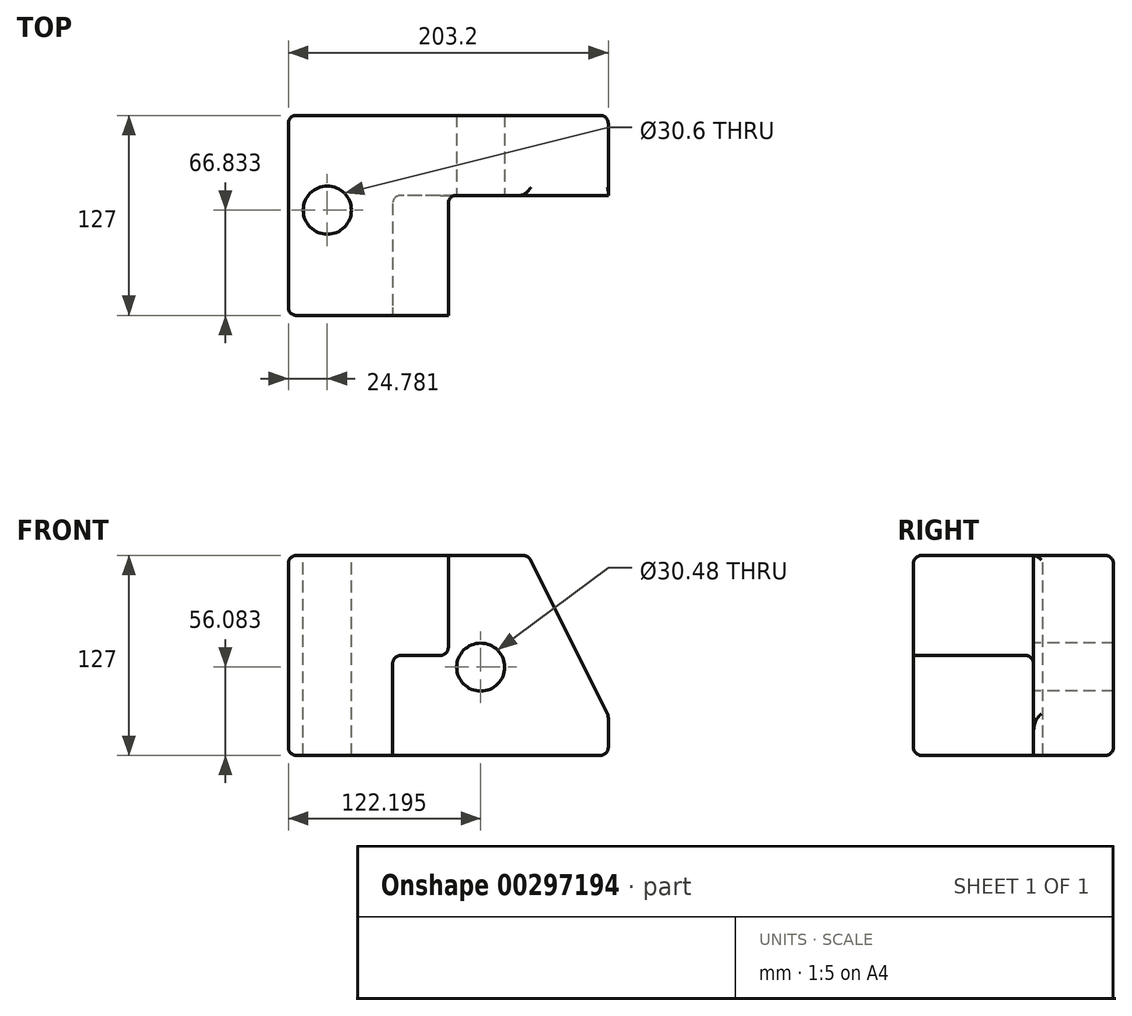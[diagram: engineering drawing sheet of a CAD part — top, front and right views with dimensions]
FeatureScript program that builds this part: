
annotation { "Feature Type Name" : "Feature", "Feature Type Description" : "" }
export const myFeature = defineFeature(function(context is Context, id is Id, definition is map)
    precondition{}
    {
        {
            var Q0;
            Q0=qCreatedBy(makeId("Front.planeOp"),FACE);
            var sketch = newSketch(context, id + "F0", { "sketchPlane" : qUnion([Q0])});
            skLineSegment(sketch, "E0.bottom", {"start": v(101.6, -63.5) * mm, "end": v(-101.6, -63.5) * mm});
            skLineSegment(sketch, "E0.top", {"start": v(101.6, 63.5) * mm, "end": v(-101.6, 63.5) * mm});
            skLineSegment(sketch, "E0.left", {"start": v(101.6, -63.5) * mm, "end": v(101.6, 63.5) * mm});
            skLineSegment(sketch, "E0.right", {"start": v(-101.6, -63.5) * mm, "end": v(-101.6, 63.5) * mm});
            skPoint(sketch, "E0.middle", {"position": v(0, 0) * mm});
            skSolve(sketch);
        }
        {
            var Q0;
            Q0=makeQuery(id+"F0.imprint","IMPRINT",FACE,{"disambiguationData":[TD([[makeQuery(id+"F0.imprint","IMPRINT",EDGE,{"derivedFrom":sQuery(id+"F0.wireOp",EDGE,"E0.bottom")}),-1.0]])]});
            extrude(context, id + "F1", {"entities" : qUnion([Q0]), "depth" : 127 * mm});
        }
        {
            var Q0;
            Q0=makeQuery(id+"F1.opExtrude","CAP_FACE",FACE,{"disambiguationData":[OSD([sQuery(id+"F0.wireOp",EDGE,"E0.bottom"),sQuery(id+"F0.wireOp",EDGE,"E0.top"),sQuery(id+"F0.wireOp",EDGE,"E0.left"),sQuery(id+"F0.wireOp",EDGE,"E0.right")])],"isStart":false});
            var sketch = newSketch(context, id + "F2", { "sketchPlane" : qUnion([Q0])});
            skLineSegment(sketch, "E1", {"start": v(-101.6, 63.5) * mm, "end": v(0, 63.5) * mm});
            skLineSegment(sketch, "E2", {"start": v(0, 63.5) * mm, "end": v(0, 0) * mm});
            skLineSegment(sketch, "E3", {"start": v(0, 0) * mm, "end": v(-35.28, 0) * mm});
            skLineSegment(sketch, "E4", {"start": v(-35.28, 0) * mm, "end": v(-35.28, -63.5) * mm});
            skLineSegment(sketch, "E5", {"start": v(-35.28, -63.5) * mm, "end": v(-101.6, -63.5) * mm});
            skLineSegment(sketch, "E6", {"start": v(-101.6, -63.5) * mm, "end": v(-101.6, 63.5) * mm});
            skSolve(sketch);
        }
        {
            var Q0;
            {var subQ3=sQuery(id+"F2.wireOp",EDGE,"E2");Q0=makeQuery(id+"F2.imprint","IMPRINT",FACE,{"disambiguationData":[TD([[makeQuery(id+"F2.imprint","IMPRINT",EDGE,{"derivedFrom":subQ3}),1.0]])]});}
            extrude(context, id + "F3", {"entities" : qUnion([Q0]), "operationType" : NewBodyOperationType.REMOVE, "oppositeDirection" : true, "depth" : 76.2 * mm});
        }
        {
            var Q0;
            Q0=makeQuery(id+"F1.opExtrude","SWEPT_EDGE",EDGE,{"disambiguationData":[OSD([sQuery(id+"F0.wireOp",EDGE,"E0.top"),sQuery(id+"F0.wireOp",EDGE,"E0.left")])]});
            chamfer(context, id + "F4", {"entities" : qUnion([Q0]), "chamferType" : ChamferType.TWO_OFFSETS, "width1" : 50.8 * mm, "oppositeDirection" : false, "width2" : 101.6 * mm, "tangentPropagation" : true});
        }
        {
            var Q0;
            Q0=makeQuery(id+"F1.opExtrude","CAP_EDGE",EDGE,{"disambiguationData":[OSD([sQuery(id+"F0.wireOp",EDGE,"E0.top")])],"isStart":false});
            var Q1;
            Q1=makeQuery(id+"F3.boolean.opBoolean","COPY",EDGE,{"derivedFrom":makeQuery(id+"F3.opExtrude","SWEPT_EDGE",EDGE,{"disambiguationData":[OSD([sQuery(id+"F0.wireOp",EDGE,"E0.top"),sQuery(id+"F2.wireOp",EDGE,"E1"),sQuery(id+"F2.wireOp",EDGE,"E2")])]})});
            var Q2;
            {var subQ0=sQuery(id+"F0.wireOp",EDGE,"E0.left");var subQ1=sQuery(id+"F0.wireOp",EDGE,"E0.top");Q2=makeQuery(id+"F4.opChamfer","BLEND_EDGE",EDGE,{"blendedFrom":[makeQuery(id+"F1.opExtrude","SWEPT_EDGE",EDGE,{"disambiguationData":[OSD([subQ1,subQ0])]}),makeQuery(id+"F3.boolean.opBoolean","COPY",FACE,{"derivedFrom":makeQuery(id+"F3.opExtrude","CAP_FACE",FACE,{"disambiguationData":[OSD([sQuery(id+"F0.wireOp",EDGE,"E0.bottom"),subQ1,subQ0,sQuery(id+"F2.wireOp",EDGE,"E2"),sQuery(id+"F2.wireOp",EDGE,"E3"),sQuery(id+"F2.wireOp",EDGE,"E4")])],"isStart":false})})],"blendedInto":[makeQuery(id+"F3.boolean.opBoolean","COPY",FACE,{"derivedFrom":makeQuery(id+"F3.opExtrude","CAP_FACE",FACE,{"disambiguationData":[OSD([sQuery(id+"F0.wireOp",EDGE,"E0.bottom"),subQ1,subQ0,sQuery(id+"F2.wireOp",EDGE,"E2"),sQuery(id+"F2.wireOp",EDGE,"E3"),sQuery(id+"F2.wireOp",EDGE,"E4")])],"isStart":false})})]});}
            var Q3;
            Q3=makeQuery(id+"F1.opExtrude","SWEPT_EDGE",EDGE,{"disambiguationData":[OSD([sQuery(id+"F0.wireOp",EDGE,"E0.top"),sQuery(id+"F0.wireOp",EDGE,"E0.right")])]});
            var Q4;
            Q4=makeQuery(id+"F1.opExtrude","CAP_EDGE",EDGE,{"disambiguationData":[OSD([sQuery(id+"F0.wireOp",EDGE,"E0.top")])],"isStart":true});
            var Q5;
            {var subQ0=sQuery(id+"F0.wireOp",EDGE,"E0.left");var subQ1=sQuery(id+"F0.wireOp",EDGE,"E0.top");Q5=makeQuery(id+"F4.opChamfer","BLEND_EDGE",EDGE,{"blendedFrom":[makeQuery(id+"F1.opExtrude","SWEPT_EDGE",EDGE,{"disambiguationData":[OSD([subQ1,subQ0])]}),makeQuery(id+"F1.opExtrude","CAP_FACE",FACE,{"disambiguationData":[OSD([sQuery(id+"F0.wireOp",EDGE,"E0.bottom"),subQ1,subQ0,sQuery(id+"F0.wireOp",EDGE,"E0.right")])],"isStart":true})],"blendedInto":[makeQuery(id+"F1.opExtrude","CAP_FACE",FACE,{"disambiguationData":[OSD([sQuery(id+"F0.wireOp",EDGE,"E0.bottom"),subQ1,subQ0,sQuery(id+"F0.wireOp",EDGE,"E0.right")])],"isStart":true})]});}
            var Q6;
            Q6=makeQuery(id+"F1.opExtrude","CAP_EDGE",EDGE,{"disambiguationData":[OSD([sQuery(id+"F0.wireOp",EDGE,"E0.bottom")])],"isStart":false});
            var Q7;
            Q7=makeQuery(id+"F1.opExtrude","SWEPT_EDGE",EDGE,{"disambiguationData":[OSD([sQuery(id+"F0.wireOp",EDGE,"E0.bottom"),sQuery(id+"F0.wireOp",EDGE,"E0.left")])]});
            var Q8;
            {var subQ0=sQuery(id+"F0.wireOp",EDGE,"E0.top");Q8=makeQuery(id+"F4.opChamfer","BLEND_EDGE",EDGE,{"blendedFrom":[makeQuery(id+"F1.opExtrude","SWEPT_EDGE",EDGE,{"disambiguationData":[OSD([subQ0,sQuery(id+"F0.wireOp",EDGE,"E0.left")])]}),makeQuery(id+"F1.opExtrude","SWEPT_FACE",FACE,{"disambiguationData":[OSD([subQ0])]})],"blendedInto":[makeQuery(id+"F1.opExtrude","SWEPT_FACE",FACE,{"disambiguationData":[OSD([subQ0])]})]});}
            var Q9;
            Q9=makeQuery(id+"F3.boolean.opBoolean","COPY",EDGE,{"derivedFrom":makeQuery(id+"F3.opExtrude","CAP_EDGE",EDGE,{"disambiguationData":[OSD([sQuery(id+"F0.wireOp",EDGE,"E0.top")])],"isStart":false})});
            var Q10;
            Q10=makeQuery(id+"F3.boolean.opBoolean","COPY",EDGE,{"derivedFrom":makeQuery(id+"F3.opExtrude","SWEPT_EDGE",EDGE,{"disambiguationData":[OSD([sQuery(id+"F2.wireOp",EDGE,"E2"),sQuery(id+"F2.wireOp",EDGE,"E3")])]})});
            var Q11;
            Q11=makeQuery(id+"F3.boolean.opBoolean","COPY",EDGE,{"derivedFrom":makeQuery(id+"F3.opExtrude","SWEPT_EDGE",EDGE,{"disambiguationData":[OSD([sQuery(id+"F0.wireOp",EDGE,"E0.bottom"),sQuery(id+"F2.wireOp",EDGE,"E4"),sQuery(id+"F2.wireOp",EDGE,"E5")])]})});
            var Q12;
            Q12=makeQuery(id+"F3.boolean.opBoolean","COPY",EDGE,{"derivedFrom":makeQuery(id+"F3.opExtrude","CAP_EDGE",EDGE,{"disambiguationData":[OSD([sQuery(id+"F2.wireOp",EDGE,"E3")])],"isStart":true})});
            var Q13;
            Q13=makeQuery(id+"F3.boolean.opBoolean","COPY",EDGE,{"derivedFrom":makeQuery(id+"F3.opExtrude","CAP_EDGE",EDGE,{"disambiguationData":[OSD([sQuery(id+"F0.wireOp",EDGE,"E0.bottom")])],"isStart":false})});
            var Q14;
            {var subQ0=sQuery(id+"F0.wireOp",EDGE,"E0.left");Q14=makeQuery(id+"F4.opChamfer","BLEND_EDGE",EDGE,{"blendedFrom":[makeQuery(id+"F1.opExtrude","SWEPT_EDGE",EDGE,{"disambiguationData":[OSD([sQuery(id+"F0.wireOp",EDGE,"E0.top"),subQ0])]}),makeQuery(id+"F1.opExtrude","SWEPT_FACE",FACE,{"disambiguationData":[OSD([subQ0])]})],"blendedInto":[makeQuery(id+"F1.opExtrude","SWEPT_FACE",FACE,{"disambiguationData":[OSD([subQ0])]})]});}
            var Q15;
            Q15=makeQuery(id+"F1.opExtrude","SWEPT_EDGE",EDGE,{"disambiguationData":[OSD([sQuery(id+"F0.wireOp",EDGE,"E0.bottom"),sQuery(id+"F0.wireOp",EDGE,"E0.right")])]});
            var Q16;
            Q16=makeQuery(id+"F1.opExtrude","CAP_EDGE",EDGE,{"disambiguationData":[OSD([sQuery(id+"F0.wireOp",EDGE,"E0.left")])],"isStart":true});
            var Q17;
            Q17=makeQuery(id+"F3.boolean.opBoolean","COPY",EDGE,{"derivedFrom":makeQuery(id+"F3.opExtrude","CAP_EDGE",EDGE,{"disambiguationData":[OSD([sQuery(id+"F2.wireOp",EDGE,"E3")])],"isStart":false})});
            var Q18;
            Q18=makeQuery(id+"F3.boolean.opBoolean","COPY",EDGE,{"derivedFrom":makeQuery(id+"F3.opExtrude","CAP_EDGE",EDGE,{"disambiguationData":[OSD([sQuery(id+"F2.wireOp",EDGE,"E2")])],"isStart":true})});
            var Q19;
            Q19=makeQuery(id+"F3.boolean.opBoolean","COPY",EDGE,{"derivedFrom":makeQuery(id+"F3.opExtrude","CAP_EDGE",EDGE,{"disambiguationData":[OSD([sQuery(id+"F2.wireOp",EDGE,"E4")])],"isStart":true})});
            var Q20;
            Q20=makeQuery(id+"F1.opExtrude","CAP_EDGE",EDGE,{"disambiguationData":[OSD([sQuery(id+"F0.wireOp",EDGE,"E0.bottom")])],"isStart":true});
            var Q21;
            Q21=makeQuery(id+"F3.boolean.opBoolean","COPY",EDGE,{"derivedFrom":makeQuery(id+"F3.opExtrude","CAP_EDGE",EDGE,{"disambiguationData":[OSD([sQuery(id+"F2.wireOp",EDGE,"E2")])],"isStart":false})});
            var Q22;
            Q22=makeQuery(id+"F3.boolean.opBoolean","COPY",EDGE,{"derivedFrom":makeQuery(id+"F3.opExtrude","CAP_EDGE",EDGE,{"disambiguationData":[OSD([sQuery(id+"F2.wireOp",EDGE,"E4")])],"isStart":false})});
            var Q23;
            Q23=makeQuery(id+"F1.opExtrude","CAP_EDGE",EDGE,{"disambiguationData":[OSD([sQuery(id+"F0.wireOp",EDGE,"E0.right")])],"isStart":false});
            var Q24;
            Q24=makeQuery(id+"F1.opExtrude","CAP_EDGE",EDGE,{"disambiguationData":[OSD([sQuery(id+"F0.wireOp",EDGE,"E0.right")])],"isStart":true});
            var Q25;
            Q25=makeQuery(id+"F3.boolean.opBoolean","COPY",EDGE,{"derivedFrom":makeQuery(id+"F3.opExtrude","SWEPT_EDGE",EDGE,{"disambiguationData":[OSD([sQuery(id+"F2.wireOp",EDGE,"E3"),sQuery(id+"F2.wireOp",EDGE,"E4")])]})});
            var Q26;
            Q26=makeQuery(id+"F3.boolean.opBoolean","COPY",EDGE,{"derivedFrom":makeQuery(id+"F3.opExtrude","CAP_EDGE",EDGE,{"disambiguationData":[OSD([sQuery(id+"F0.wireOp",EDGE,"E0.left")])],"isStart":false})});
            fillet(context, id + "F5", {"entities" : qUnion([Q0, Q1, Q2, Q3, Q4, Q5, Q6, Q7, Q8, Q9, Q10, Q11, Q12, Q13, Q14, Q15, Q16, Q17, Q18, Q19, Q20, Q21, Q22, Q23, Q24, Q25, Q26]), "radius" : 5.08 * mm, "tangentPropagation" : true, "allowEdgeOverflow" : false});
        }
        {
            var Q0;
            Q0=makeQuery(id+"F3.boolean.opBoolean","COPY",FACE,{"derivedFrom":makeQuery(id+"F3.opExtrude","CAP_FACE",FACE,{"disambiguationData":[OSD([sQuery(id+"F0.wireOp",EDGE,"E0.bottom"),sQuery(id+"F0.wireOp",EDGE,"E0.top"),sQuery(id+"F0.wireOp",EDGE,"E0.left"),sQuery(id+"F2.wireOp",EDGE,"E2"),sQuery(id+"F2.wireOp",EDGE,"E3"),sQuery(id+"F2.wireOp",EDGE,"E4")])],"isStart":false})});
            var sketch = newSketch(context, id + "F6", { "sketchPlane" : qUnion([Q0])});
            skCircle(sketch, "E7", {"center": v(20.6, -7.42) * mm, "radius": 15.24 * mm});
            skSolve(sketch);
        }
        {
            var Q0;
            Q0=makeQuery(id+"F6.imprint","IMPRINT",FACE,{"disambiguationData":[TD([[makeQuery(id+"F6.imprint","IMPRINT",EDGE,{"derivedFrom":sQuery(id+"F6.wireOp",EDGE,"E7")}),1.0]])]});
            var Q1;
            Q1=sQuery(id+"F6.wireOp",EDGE,"E7");
            var Q2;
            Q2=makeQuery(id+"F1.opExtrude","CAP_FACE",FACE,{"disambiguationData":[OSD([sQuery(id+"F0.wireOp",EDGE,"E0.bottom"),sQuery(id+"F0.wireOp",EDGE,"E0.top"),sQuery(id+"F0.wireOp",EDGE,"E0.left"),sQuery(id+"F0.wireOp",EDGE,"E0.right")])],"isStart":true});
            extrude(context, id + "F7", {"entities" : qUnion([Q0]), "operationType" : NewBodyOperationType.REMOVE, "surfaceEntities" : qUnion([Q1]), "endBound" : BoundingType.UP_TO_SURFACE, "oppositeDirection" : true, "endBoundEntityFace" : qUnion([Q2]), "depth" : 25.4 * mm});
        }
        {
            var Q0;
            Q0=makeQuery(id+"F1.opExtrude","SWEPT_FACE",FACE,{"disambiguationData":[OSD([sQuery(id+"F0.wireOp",EDGE,"E0.top")])]});
            var sketch = newSketch(context, id + "F8", { "sketchPlane" : qUnion([Q0])});
            skCircle(sketch, "E8", {"center": v(-76.82, -60.17) * mm, "radius": 15.3 * mm});
            skSolve(sketch);
        }
        {
            var Q0;
            Q0=makeQuery(id+"F8.imprint","IMPRINT",FACE,{"disambiguationData":[TD([[makeQuery(id+"F8.imprint","IMPRINT",EDGE,{"derivedFrom":sQuery(id+"F8.wireOp",EDGE,"E8")}),1.0]])]});
            var Q1;
            Q1=makeQuery(id+"F1.opExtrude","SWEPT_FACE",FACE,{"disambiguationData":[OSD([sQuery(id+"F0.wireOp",EDGE,"E0.bottom")])]});
            extrude(context, id + "F9", {"entities" : qUnion([Q0]), "operationType" : NewBodyOperationType.REMOVE, "endBound" : BoundingType.UP_TO_SURFACE, "oppositeDirection" : true, "endBoundEntityFace" : qUnion([Q1]), "depth" : 25.4 * mm});
        }
    });
